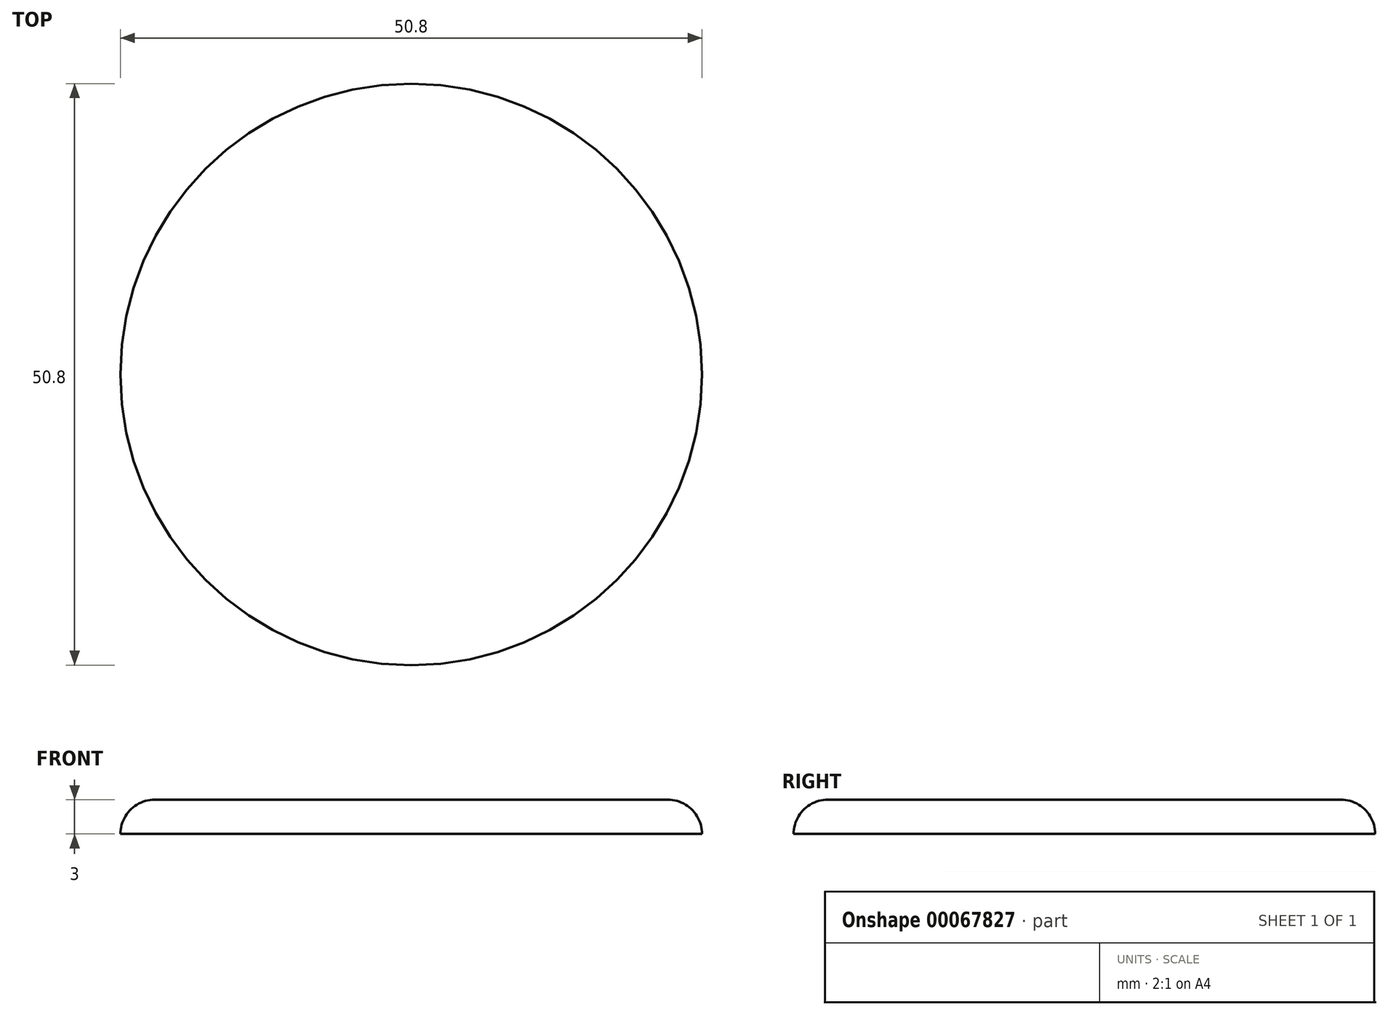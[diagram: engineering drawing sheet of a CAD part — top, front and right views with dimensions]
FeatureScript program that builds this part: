
annotation { "Feature Type Name" : "Feature", "Feature Type Description" : "" }
export const myFeature = defineFeature(function(context is Context, id is Id, definition is map)
    precondition{}
    {
        {
            var Q0;
            Q0=qCreatedBy(makeId("Top.planeOp"),FACE);
            var sketch = newSketch(context, id + "F0", { "sketchPlane" : qUnion([Q0])});
            skCircle(sketch, "E0", {"center": v(0, 0) * mm, "radius": 25.4 * mm});
            skSolve(sketch);
        }
        {
            var Q0;
            Q0=makeQuery(id+"F0.imprint","IMPRINT",FACE,{"disambiguationData":[TD([[makeQuery(id+"F0.imprint","IMPRINT",EDGE,{"derivedFrom":sQuery(id+"F0.wireOp",EDGE,"E0")}),1.0]])]});
            extrude(context, id + "F1", {"entities" : qUnion([Q0]), "oppositeDirection" : true, "depth" : 3 * mm});
        }
        {
            var Q0;
            Q0=makeQuery(id+"F1.opExtrude","CAP_EDGE",EDGE,{"disambiguationData":[OSD([sQuery(id+"F0.wireOp",EDGE,"E0")])],"isStart":true});
            fillet(context, id + "F2", {"entities" : qUnion([Q0]), "radius" : 3 * mm, "tangentPropagation" : true, "allowEdgeOverflow" : false});
        }
    });
